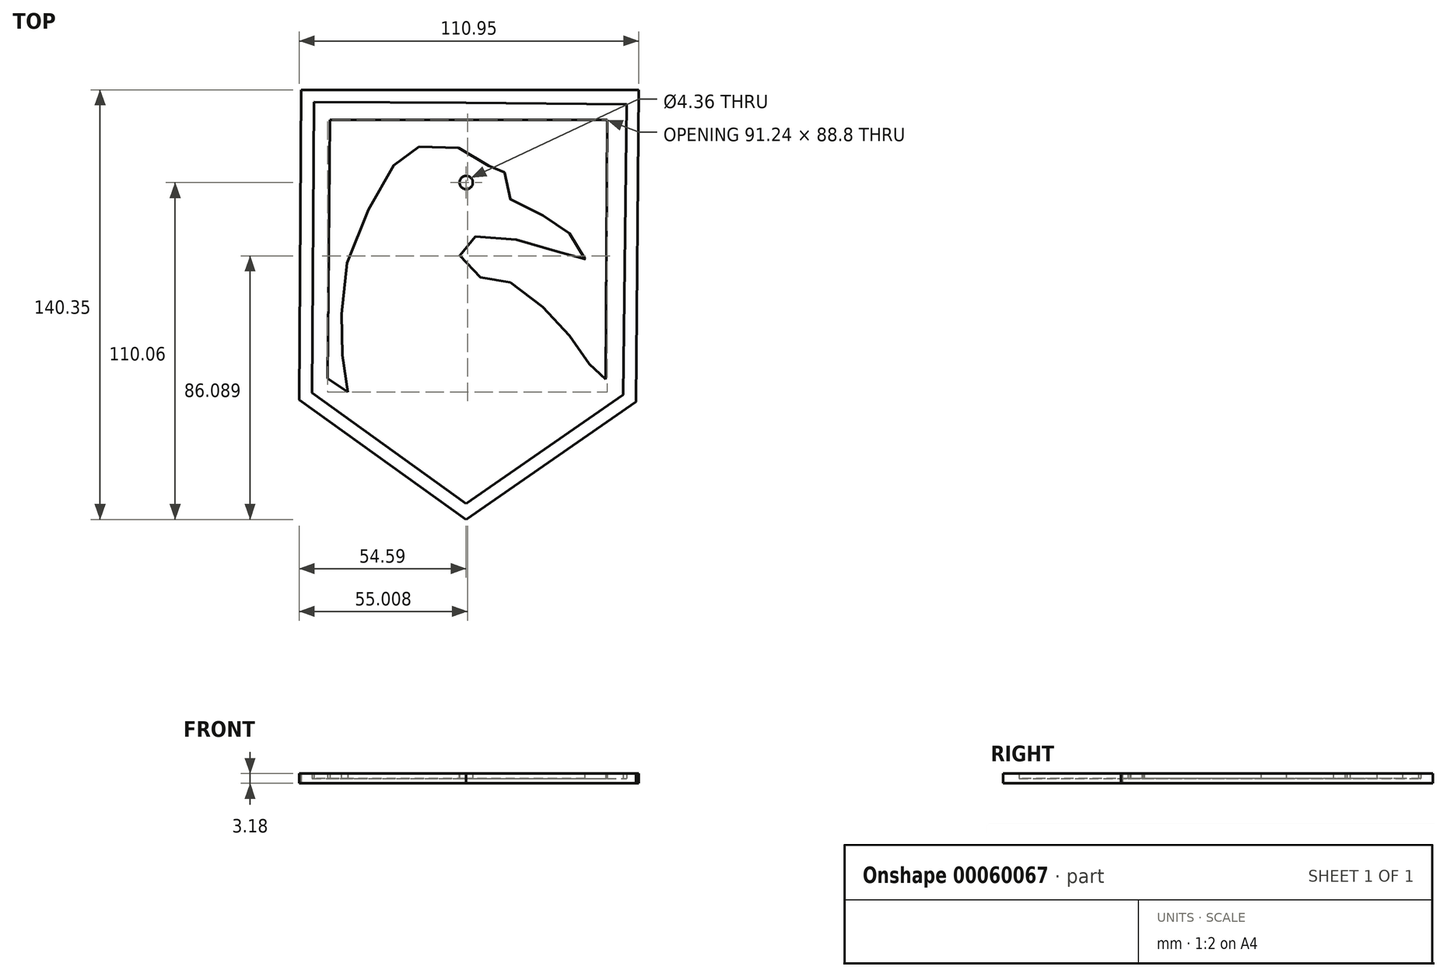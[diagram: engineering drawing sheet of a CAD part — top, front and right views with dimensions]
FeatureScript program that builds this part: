
annotation { "Feature Type Name" : "Feature", "Feature Type Description" : "" }
export const myFeature = defineFeature(function(context is Context, id is Id, definition is map)
    precondition{}
    {
        {
            var Q0;
            Q0=qCreatedBy(makeId("Top.planeOp"),FACE);
            var sketch = newSketch(context, id + "F0", { "sketchPlane" : qUnion([Q0])});
            skLineSegment(sketch, "E0", {"start": v(0, 65.12) * mm, "end": v(56.36, 65.12) * mm});
            skLineSegment(sketch, "E1", {"start": v(55.42, -36.73) * mm, "end": v(56.36, 65.12) * mm});
            skLineSegment(sketch, "E2", {"start": v(0, -75.23) * mm, "end": v(55.42, -36.73) * mm});
            skLineSegment(sketch, "E3", {"start": v(0, -70.05) * mm, "end": v(51.25, -34.45) * mm});
            skLineSegment(sketch, "E4", {"start": v(51.25, -34.45) * mm, "end": v(52.37, 60.42) * mm});
            skLineSegment(sketch, "E5", {"start": v(0, 60.9) * mm, "end": v(52.37, 60.42) * mm});
            skLineSegment(sketch, "E6", {"start": v(-44.54, 55.26) * mm, "end": v(46.04, 55.26) * mm});
            skLineSegment(sketch, "E7", {"start": v(46.04, 55.26) * mm, "end": v(45.56, -29.45) * mm});
            skLineSegment(sketch, "E8", {"start": v(-44.54, 55.26) * mm, "end": v(-45.2, -29.12) * mm});
            skLineSegment(sketch, "E9", {"start": v(-45.2, -29.12) * mm, "end": v(-38.68, -33.54) * mm});
            skFitSpline(sketch, "E10", {"points": [v(-38.62, -34.39) * mm, v(-39.34, -28.88) * mm, v(-40.21, -24.38) * mm, v(-40.45, -18.3) * mm, v(-40.74, -11.99) * mm, v(-40.5, -4.71) * mm, v(-39.57, 5.61) * mm, v(-35.35, 18.28) * mm, v(-30.65, 28.6) * mm, v(-25.72, 37.53) * mm, v(-21.03, 43.63) * mm, v(-18.68, 45.5) * mm, v(-15.87, 46.44) * mm, v(-8.36, 46.91) * mm, v(-3.9, 46.44) * mm, v(2.67, 44.57) * mm, v(6.19, 41.98) * mm, v(7.83, 39.4) * mm, v(9.48, 36.6) * mm, v(10.88, 37.53) * mm, v(12.06, 38.22) * mm, v(12.99, 37.53) * mm, v(13.46, 34.48) * mm, v(13.93, 31.43) * mm, v(15.1, 28.14) * mm, v(20.03, 26.03) * mm, v(25.43, 23.92) * mm, v(28.95, 22.27) * mm, v(32.47, 19.7) * mm, v(34.82, 16.64) * mm, v(36.7, 13.36) * mm, v(38.34, 10.77) * mm, v(38.8, 9.14) * mm, v(36.7, 9.84) * mm, v(31.77, 11.48) * mm, v(25.9, 13.83) * mm, v(18.63, 15.7) * mm, v(11.12, 17.11) * mm, v(4.08, 17.34) * mm, v(1.73, 16.88) * mm, v(-2.02, 15.23) * mm, v(-2.02, 12.18) * mm, v(-2.02, 9.13) * mm, v(2.2, 5.14) * mm, v(4.31, 3.97) * mm, v(7.83, 3.73) * mm, v(11.35, 3.03) * mm, v(14.64, 2.1) * mm, v(20.74, -2.37) * mm, v(24.73, -5.65) * mm, v(28.95, -9.64) * mm, v(32.94, -14.33) * mm, v(36.23, -18.32) * mm, v(38.8, -21.84) * mm, v(40.92, -25.36) * mm, v(42.56, -26.77) * mm, v(43.27, -29.45) * mm, v(45.56, -29.45) * mm], "startDerivative": vector(-10.99, 224.07) * mm, "endDerivative": vector(225.38, 57.8) * mm});
            skLineSegment(sketch, "E11", {"start": v(0, 65.12) * mm, "end": v(-53.89, 65.12) * mm});
            skLineSegment(sketch, "E12", {"start": v(-53.89, 65.12) * mm, "end": v(-54.59, -36.16) * mm});
            skLineSegment(sketch, "E13", {"start": v(-54.59, -36.16) * mm, "end": v(0, -75.23) * mm});
            skLineSegment(sketch, "E14", {"start": v(0, 60.9) * mm, "end": v(-49.66, 61.17) * mm});
            skLineSegment(sketch, "E15", {"start": v(-49.66, 61.17) * mm, "end": v(-50.37, -33.81) * mm});
            skLineSegment(sketch, "E16", {"start": v(-50.37, -33.81) * mm, "end": v(0, -70.05) * mm});
            skCircle(sketch, "E17", {"center": v(0, 34.83) * mm, "radius": 2.18 * mm});
            skSolve(sketch);
        }
        {
            var Q0;
            Q0=makeQuery(id+"F0.imprint","IMPRINT",FACE,{"disambiguationData":[TD([[makeQuery(id+"F0.imprint","IMPRINT",EDGE,{"derivedFrom":sQuery(id+"F0.wireOp",EDGE,"E3")}),1.0]])]});
            var Q1;
            Q1=makeQuery(id+"F0.imprint","IMPRINT",FACE,{"disambiguationData":[TD([[makeQuery(id+"F0.imprint","IMPRINT",EDGE,{"derivedFrom":sQuery(id+"F0.wireOp",EDGE,"E6")}),-1.0]])]});
            extrude(context, id + "F1", {"entities" : qUnion([Q0, Q1]), "oppositeDirection" : true, "depth" : 1.59 * mm});
        }
        {
            var Q0;
            Q0=makeQuery(id+"F0.imprint","IMPRINT",FACE,{"disambiguationData":[TD([[makeQuery(id+"F0.imprint","IMPRINT",EDGE,{"derivedFrom":sQuery(id+"F0.wireOp",EDGE,"E0")}),-1.0]])]});
            var Q1;
            Q1=makeQuery(id+"F0.imprint","IMPRINT",FACE,{"disambiguationData":[TD([[makeQuery(id+"F0.imprint","IMPRINT",EDGE,{"derivedFrom":sQuery(id+"F0.wireOp",EDGE,"E17")}),1.0]])]});
            extrude(context, id + "F2", {"entities" : qUnion([Q0, Q1]), "operationType" : NewBodyOperationType.ADD, "depth" : 1.59 * mm, "hasSecondDirection" : true, "secondDirectionOppositeDirection" : true, "secondDirectionDepth" : 1.59 * mm});
        }
        {
            var Q0;
            Q0=makeQuery(id+"F0.imprint","IMPRINT",FACE,{"disambiguationData":[TD([[makeQuery(id+"F0.imprint","IMPRINT",EDGE,{"derivedFrom":sQuery(id+"F0.wireOp",EDGE,"E3")}),1.0]])]});
            extrude(context, id + "F3", {"entities" : qUnion([Q0]), "depth" : 1.59 * mm});
        }
    });
